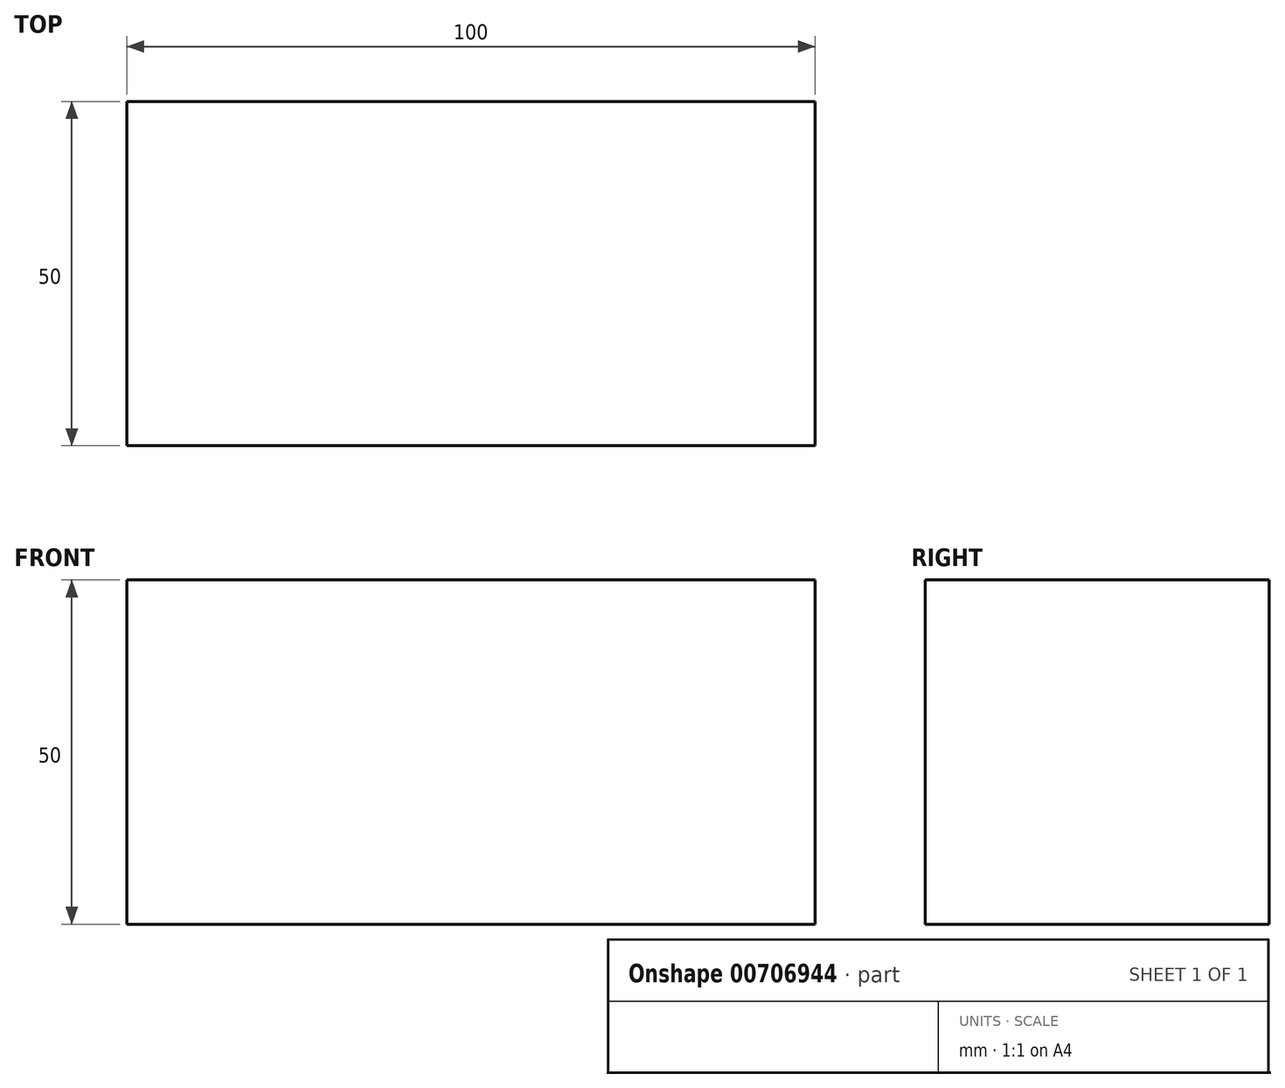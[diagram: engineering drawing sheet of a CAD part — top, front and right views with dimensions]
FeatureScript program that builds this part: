
annotation { "Feature Type Name" : "Feature", "Feature Type Description" : "" }
export const myFeature = defineFeature(function(context is Context, id is Id, definition is map)
    precondition{}
    {
        {
            var Q0;
            Q0=qCreatedBy(makeId("Front.planeOp"),FACE);
            var sketch = newSketch(context, id + "F0", { "sketchPlane" : qUnion([Q0])});
            skLineSegment(sketch, "E0.bottom", {"start": v(-49.3, 25.87) * mm, "end": v(50.7, 25.87) * mm});
            skLineSegment(sketch, "E0.top", {"start": v(-49.3, -24.13) * mm, "end": v(50.7, -24.13) * mm});
            skLineSegment(sketch, "E0.left", {"start": v(-49.3, 25.87) * mm, "end": v(-49.3, -24.13) * mm});
            skLineSegment(sketch, "E0.right", {"start": v(50.7, 25.87) * mm, "end": v(50.7, -24.13) * mm});
            skSolve(sketch);
        }
        {
            var Q0;
            Q0 = qSketchRegion(id + "F0", true);
            extrude(context, id + "F1", {"entities" : qUnion([Q0]), "depth" : 50 * mm, "offsetDistance" : 25 * mm});
        }
    });
